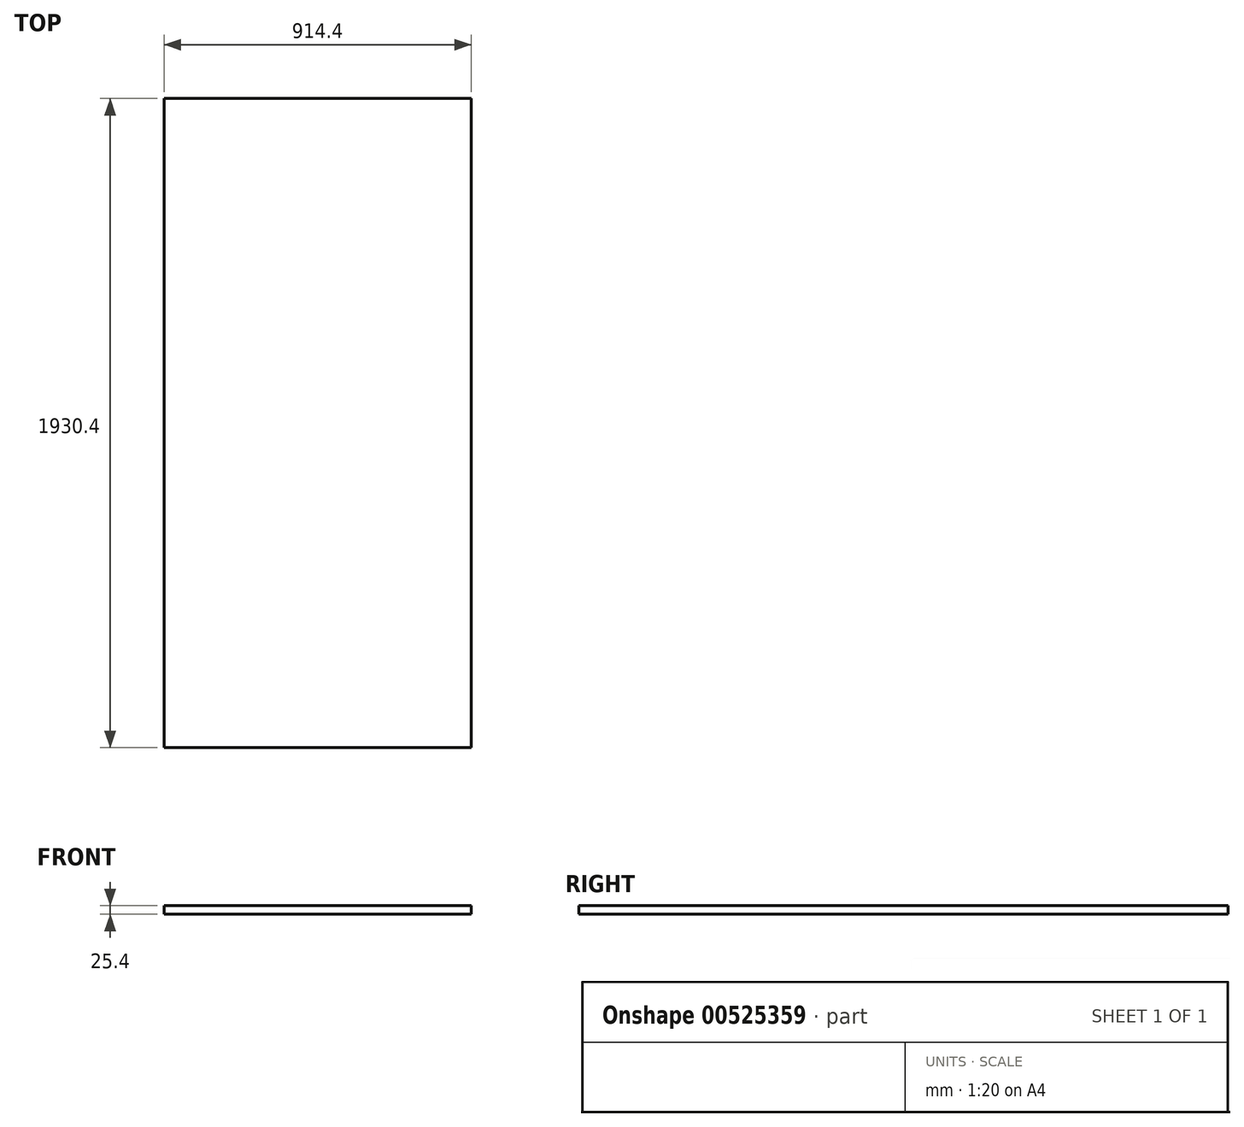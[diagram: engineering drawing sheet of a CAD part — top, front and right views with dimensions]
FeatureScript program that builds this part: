
annotation { "Feature Type Name" : "Feature", "Feature Type Description" : "" }
export const myFeature = defineFeature(function(context is Context, id is Id, definition is map)
    precondition{}
    {
        {
            var Q0;
            Q0=qCreatedBy(makeId("Front.planeOp"),FACE);
            var sketch = newSketch(context, id + "F0", { "sketchPlane" : qUnion([Q0])});
            skLineSegment(sketch, "E0.bottom", {"start": v(-447.35, 25.4) * mm, "end": v(467.05, 25.4) * mm});
            skLineSegment(sketch, "E0.top", {"start": v(-447.35, 0) * mm, "end": v(467.05, 0) * mm});
            skLineSegment(sketch, "E0.left", {"start": v(-447.35, 25.4) * mm, "end": v(-447.35, 0) * mm});
            skLineSegment(sketch, "E0.right", {"start": v(467.05, 25.4) * mm, "end": v(467.05, 0) * mm});
            skSolve(sketch);
        }
        {
            var Q0;
            Q0=makeQuery(id+"F0.imprint","IMPRINT",FACE,{"disambiguationData":[TD([[makeQuery(id+"F0.imprint","IMPRINT",EDGE,{"derivedFrom":sQuery(id+"F0.wireOp",EDGE,"E0.bottom")}),-1.0]])]});
            extrude(context, id + "F1", {"entities" : qUnion([Q0]), "oppositeDirection" : true, "depth" : 1930.4 * mm, "offsetDistance" : 25.4 * mm});
        }
    });
